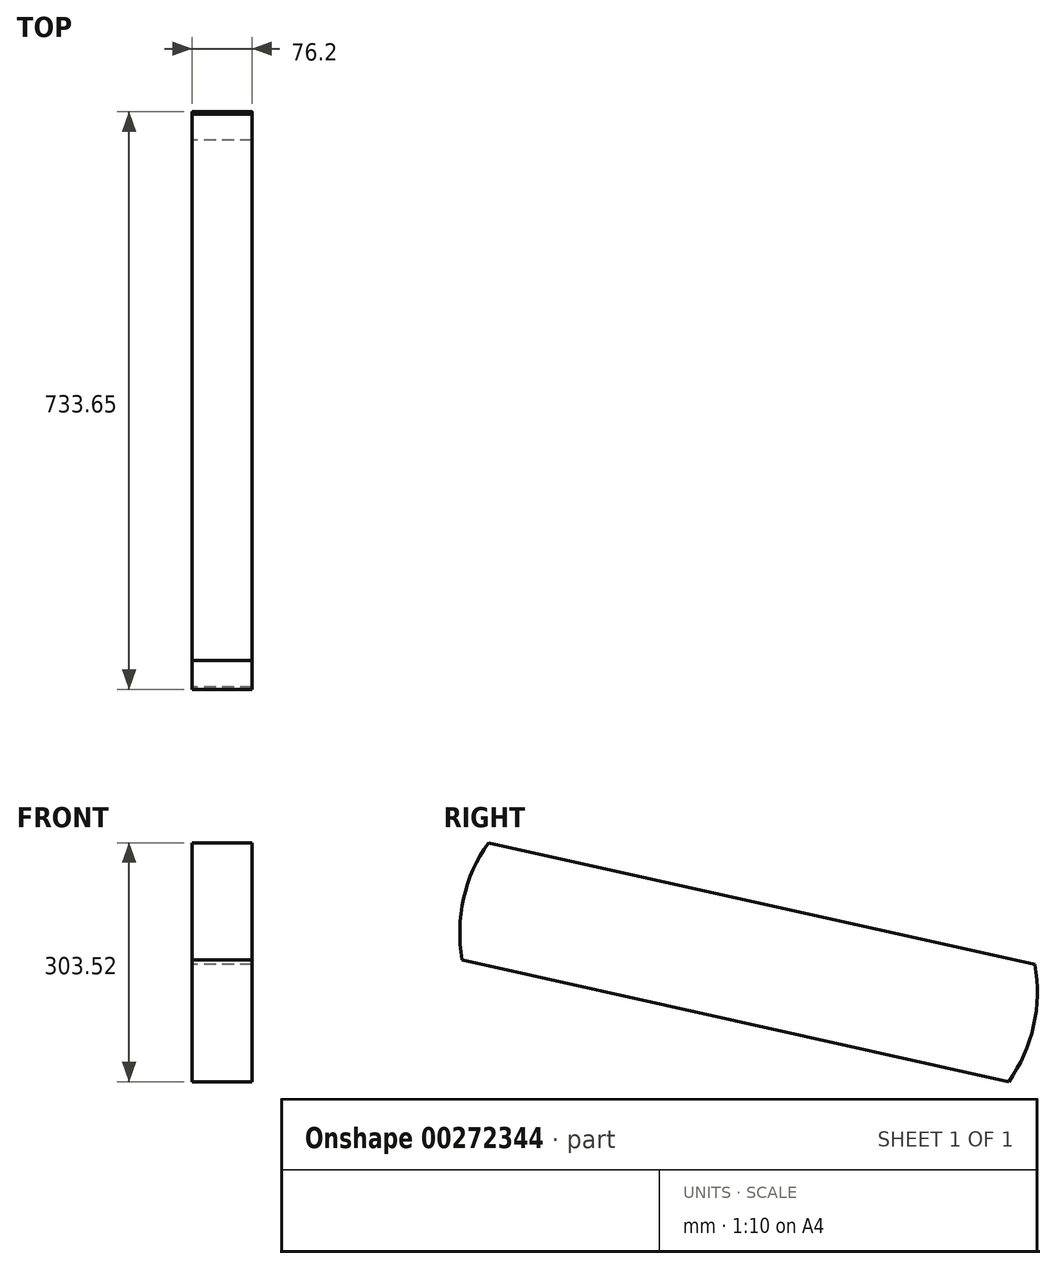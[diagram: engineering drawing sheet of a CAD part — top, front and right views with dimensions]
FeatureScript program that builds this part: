
annotation { "Feature Type Name" : "Feature", "Feature Type Description" : "" }
export const myFeature = defineFeature(function(context is Context, id is Id, definition is map)
    precondition{}
    {
        {
            var Q0;
            Q0=qCreatedBy(makeId("Right.planeOp"),FACE);
            var sketch = newSketch(context, id + "F0", { "sketchPlane" : qUnion([Q0])});
            skLineSegment(sketch, "E0", {"start": v(311.56, -124.18) * mm, "end": v(-382.6, 30.59) * mm});
            skLineSegment(sketch, "E1", {"start": v(344.73, 24.57) * mm, "end": v(-349.43, 179.34) * mm});
            skArc(sketch, "E2", {"start": v(311.56, -124.18) * mm, "mid": v(343.2, -53.16) * mm, "end": v(344.73, 24.57) * mm});
            skArc(sketch, "E3", {"start": v(-349.43, 179.34) * mm, "mid": v(-381.06, 108.32) * mm, "end": v(-382.6, 30.59) * mm});
            skLineSegment(sketch, "E4", {"start": v(-349.43, 179.34) * mm, "end": v(-382.6, 30.59) * mm, "construction": true});
            skLineSegment(sketch, "E5", {"start": v(-382.5, 108.64) * mm, "end": v(314.32, -46.72) * mm, "construction": true});
            skLineSegment(sketch, "E6", {"start": v(344.73, 24.57) * mm, "end": v(311.56, -124.18) * mm, "construction": true});
            skSolve(sketch);
        }
        {
            var Q0;
            Q0=makeQuery(id+"F0.imprint","IMPRINT",FACE,{"disambiguationData":[TD([[makeQuery(id+"F0.imprint","IMPRINT",EDGE,{"derivedFrom":sQuery(id+"F0.wireOp",EDGE,"E0")}),-1.0]])]});
            extrude(context, id + "F1", {"entities" : qUnion([Q0]), "depth" : 76.2 * mm});
        }
    });
